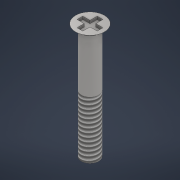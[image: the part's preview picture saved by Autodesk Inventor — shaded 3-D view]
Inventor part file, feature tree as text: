
AUTODESK INVENTOR PART (.ipt)
format: ipt  version: 2021 (Build 250183000, 183)  size: 140,800 bytes
history: native  units: mm
features: other x4, sketch x3, extrude x2, loft x1, thread x1
ambient origin geometry x8: Origin, YZ Plane, XZ Plane, XY Plane, X Axis, Y Axis, Z Axis, Center Point
bodies: Body1 (feature_tree)
feature tree (11):
  other  "Parafuso"
  other  "Sólido1"
  extrude  "Extrusão1"  Depth=9.6mm TaperAngle=0.0deg
  other  "Plano de trabalho1"
  loft  "Transição1"
  extrude  "Extrusão2"  TaperAngle=0.0deg  [1 undecoded]
  thread  "Rosca1"  [1 undecoded]
  sketch  "Esboço1"  dims[d1=1.5mm d2=9.6mm d3=0.0mm]
  sketch  "Esboço2"  dims[d4=0.4mm d5=2.5mm]
  other  "Arestas1"
  sketch  "Esboço3"  dims[d6=0.0mm d7=90.0deg d8=0.0mm d9=90.0deg d10=0.5mm d11=1.75mm d14=1.75mm d15=0.5mm d16=0.25mm d17=0.0mm d18=5.0mm d19=0.0mm d20=0.5mm d21=0.872665mm d22=0.5mm d23=0.872665mm]
note: 2 required parameter values undecoded (feature->parameter linkage not recoverable at this tier; creation-order binding heuristic only, values carry confidence <= 0.55)
